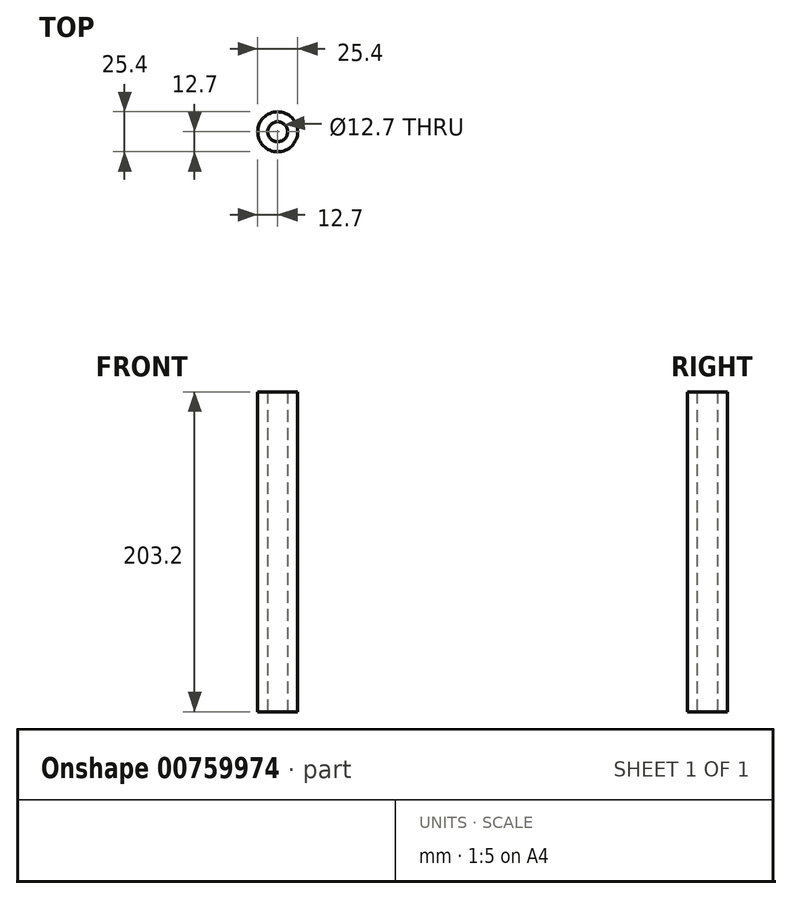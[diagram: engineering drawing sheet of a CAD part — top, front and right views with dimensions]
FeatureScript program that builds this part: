
annotation { "Feature Type Name" : "Feature", "Feature Type Description" : "" }
export const myFeature = defineFeature(function(context is Context, id is Id, definition is map)
    precondition{}
    {
        {
            var Q0;
            Q0=qCreatedBy(makeId("Top.planeOp"),FACE);
            var sketch = newSketch(context, id + "F0", { "sketchPlane" : qUnion([Q0])});
            skCircle(sketch, "E0", {"center": v(0, 0) * mm, "radius": 12.7 * mm});
            skCircle(sketch, "E1", {"center": v(0, 0) * mm, "radius": 6.35 * mm});
            skSolve(sketch);
        }
        {
            var Q0;
            Q0=makeQuery(id+"F0.imprint","IMPRINT",FACE,{"disambiguationData":[TD([[makeQuery(id+"F0.imprint","IMPRINT",EDGE,{"derivedFrom":sQuery(id+"F0.wireOp",EDGE,"E0")}),1.0]])]});
            extrude(context, id + "F1", {"entities" : qUnion([Q0]), "depth" : 203.2 * mm, "offsetDistance" : 25.4 * mm});
        }
    });
